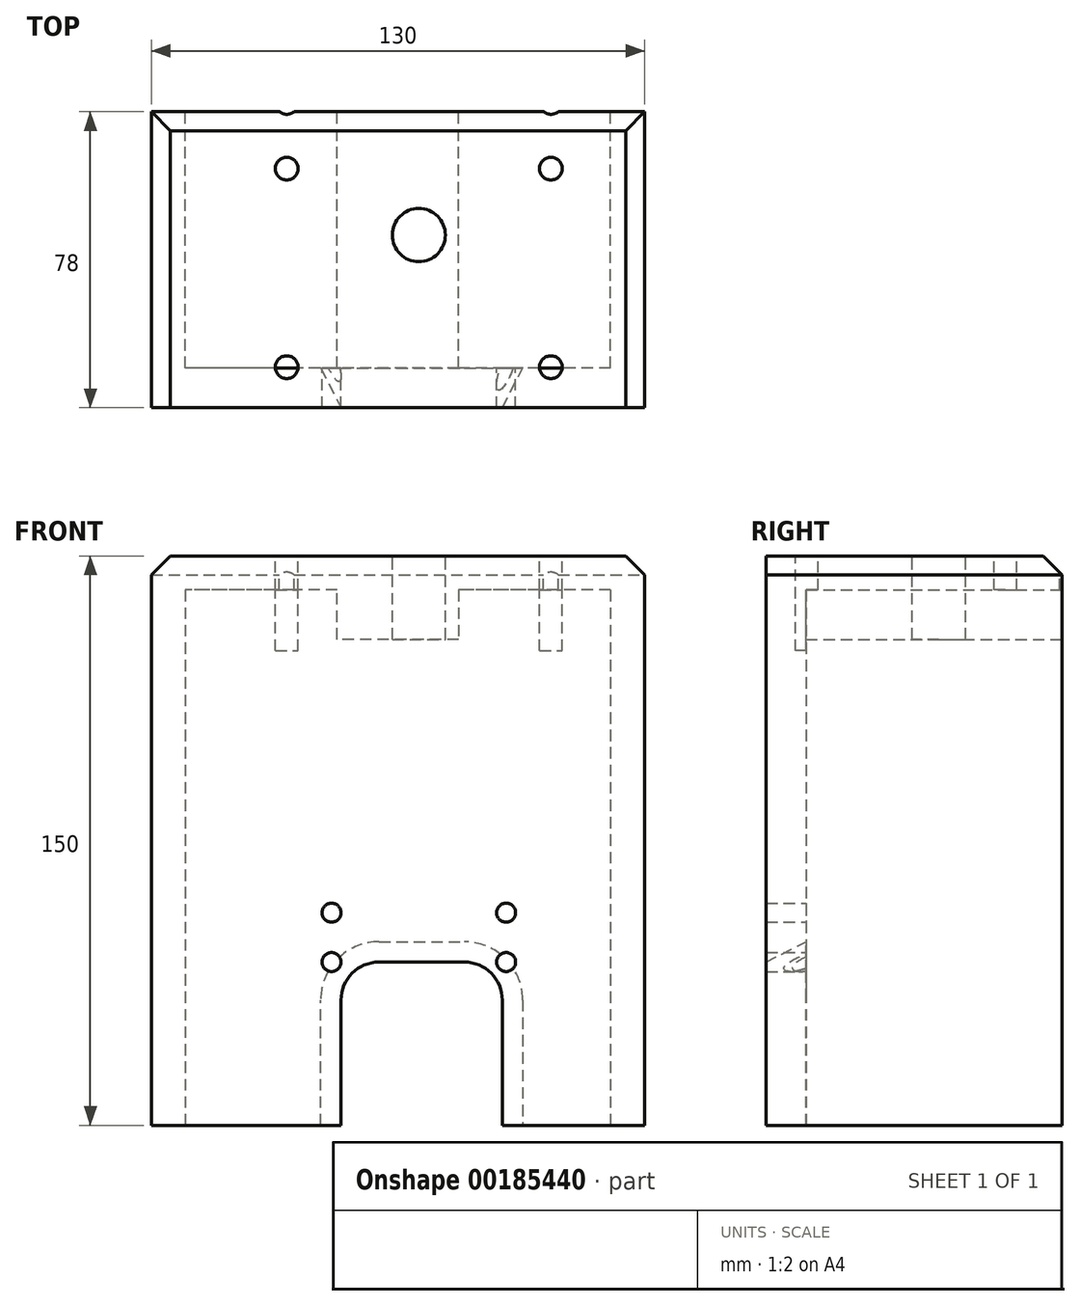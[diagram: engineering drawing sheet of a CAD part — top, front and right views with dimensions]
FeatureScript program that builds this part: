
annotation { "Feature Type Name" : "Feature", "Feature Type Description" : "" }
export const myFeature = defineFeature(function(context is Context, id is Id, definition is map)
    precondition{}
    {
        {
            var Q0;
            Q0=qCreatedBy(makeId("Top.planeOp"),FACE);
            var sketch = newSketch(context, id + "F0", { "sketchPlane" : qUnion([Q0])});
            skLineSegment(sketch, "E0.bottom", {"start": v(65, 39) * mm, "end": v(-65, 39) * mm});
            skLineSegment(sketch, "E0.top", {"start": v(65, -39) * mm, "end": v(-65, -39) * mm});
            skLineSegment(sketch, "E0.left", {"start": v(65, 39) * mm, "end": v(65, -39) * mm});
            skLineSegment(sketch, "E0.right", {"start": v(-65, 39) * mm, "end": v(-65, -39) * mm});
            skPoint(sketch, "E0.middle", {"position": v(0, 0) * mm});
            skSolve(sketch);
        }
        {
            var Q0;
            Q0=makeQuery(id+"F0.imprint","IMPRINT",FACE,{"disambiguationData":[TD([[makeQuery(id+"F0.imprint","IMPRINT",EDGE,{"derivedFrom":sQuery(id+"F0.wireOp",EDGE,"E0.bottom")}),1.0]])]});
            extrude(context, id + "F14", {"entities" : qUnion([Q0]), "oppositeDirection" : true, "depth" : 150 * mm});
        }
        {
            var Q0;
            Q0=makeQuery(id+"F14.opExtrude","SWEPT_FACE",FACE,{"disambiguationData":[OSD([sQuery(id+"F0.wireOp",EDGE,"E0.bottom")])]});
            var sketch = newSketch(context, id + "F15", { "sketchPlane" : qUnion([Q0])});
            skLineSegment(sketch, "E1.bottom", {"start": v(-56, -9) * mm, "end": v(-16, -9) * mm});
            skLineSegment(sketch, "E1.top", {"start": v(-56, -150) * mm, "end": v(56, -150) * mm});
            skLineSegment(sketch, "E1.left", {"start": v(-56, -9) * mm, "end": v(-56, -150) * mm});
            skLineSegment(sketch, "E1.right", {"start": v(56, -9) * mm, "end": v(56, -150) * mm});
            skLineSegment(sketch, "E2", {"start": v(-16, -9) * mm, "end": v(-16, -22) * mm});
            skLineSegment(sketch, "E3", {"start": v(-16, -22) * mm, "end": v(16, -22) * mm});
            skLineSegment(sketch, "E4", {"start": v(16, -22) * mm, "end": v(16, -9) * mm});
            skLineSegment(sketch, "E5.trimOffspring", {"start": v(16, -9) * mm, "end": v(56, -9) * mm});
            skSolve(sketch);
        }
        {
            var Q0;
            Q0=makeQuery(id+"F14.opExtrude","CAP_EDGE",EDGE,{"disambiguationData":[OSD([sQuery(id+"F0.wireOp",EDGE,"E0.left")])],"isStart":true});
            var Q1;
            Q1=makeQuery(id+"F14.opExtrude","CAP_EDGE",EDGE,{"disambiguationData":[OSD([sQuery(id+"F0.wireOp",EDGE,"E0.right")])],"isStart":true});
            var Q2;
            Q2=makeQuery(id+"F14.opExtrude","CAP_EDGE",EDGE,{"disambiguationData":[OSD([sQuery(id+"F0.wireOp",EDGE,"E0.bottom")])],"isStart":true});
            chamfer(context, id + "F1", {"entities" : qUnion([Q0, Q1, Q2]), "width" : 5 * mm, "tangentPropagation" : true});
        }
        {
            var Q0;
            Q0=makeQuery(id+"F15.imprint","IMPRINT",FACE,{"disambiguationData":[TD([[makeQuery(id+"F15.imprint","IMPRINT",EDGE,{"derivedFrom":sQuery(id+"F15.wireOp",EDGE,"E1.bottom")}),-1.0]])]});
            extrude(context, id + "F2", {"entities" : qUnion([Q0]), "operationType" : NewBodyOperationType.REMOVE, "oppositeDirection" : true, "depth" : 67.5 * mm});
        }
        {
            var Q0;
            Q0=makeQuery(id+"F14.opExtrude","CAP_FACE",FACE,{"disambiguationData":[OSD([sQuery(id+"F0.wireOp",EDGE,"E0.bottom"),sQuery(id+"F0.wireOp",EDGE,"E0.top"),sQuery(id+"F0.wireOp",EDGE,"E0.left"),sQuery(id+"F0.wireOp",EDGE,"E0.right")])],"isStart":true});
            var sketch = newSketch(context, id + "F3", { "sketchPlane" : qUnion([Q0])});
            skCircle(sketch, "E6", {"center": v(-34.8, -29) * mm, "radius": 3 * mm});
            skCircle(sketch, "E7", {"center": v(-34.8, 40.6) * mm, "radius": 3 * mm});
            skPoint(sketch, "E8.center.orphan", {"position": v(0, 5.8) * mm});
            skSolve(sketch);
        }
        {
            var Q0;
            Q0=makeQuery(id+"F3.imprint","IMPRINT",FACE,{"disambiguationData":[TD([[makeQuery(id+"F3.imprint","IMPRINT",EDGE,{"derivedFrom":sQuery(id+"F3.wireOp",EDGE,"E6")}),-1.0]])]});
            var sketch = newSketch(context, id + "F4", { "sketchPlane" : qUnion([Q0])});
            skCircle(sketch, "E9", {"center": v(5.5, 6.5) * mm, "radius": 6 * mm});
            skSolve(sketch);
        }
        {
            var Q0;
            Q0=makeQuery(id+"F4.imprint","IMPRINT",FACE,{"disambiguationData":[TD([[makeQuery(id+"F4.imprint","IMPRINT",EDGE,{"derivedFrom":sQuery(id+"F4.wireOp",EDGE,"E9")}),1.0]])]});
            extrude(context, id + "F5", {"entities" : qUnion([Q0]), "operationType" : NewBodyOperationType.REMOVE, "endBound" : BoundingType.THROUGH_ALL, "oppositeDirection" : true, "depth" : 25 * mm});
        }
        {
            var Q0;
            Q0=makeQuery(id+"F14.opExtrude","CAP_FACE",FACE,{"disambiguationData":[OSD([sQuery(id+"F0.wireOp",EDGE,"E0.bottom"),sQuery(id+"F0.wireOp",EDGE,"E0.top"),sQuery(id+"F0.wireOp",EDGE,"E0.left"),sQuery(id+"F0.wireOp",EDGE,"E0.right")])],"isStart":true});
            var sketch = newSketch(context, id + "F6", { "sketchPlane" : qUnion([Q0])});
            skCircle(sketch, "E10", {"center": v(5.5, 6.5) * mm, "radius": 7 * mm});
            skCircle(sketch, "E11", {"center": v(-29.3, -28.3) * mm, "radius": 3 * mm});
            skCircle(sketch, "E12", {"center": v(-29.3, 41.3) * mm, "radius": 3 * mm});
            skCircle(sketch, "E13", {"center": v(40.3, 41.3) * mm, "radius": 3 * mm});
            skCircle(sketch, "E14", {"center": v(40.3, -28.3) * mm, "radius": 3 * mm});
            skSolve(sketch);
        }
        {
            var Q0;
            Q0 = qSketchRegion(id + "F6", true);
            extrude(context, id + "F7", {"entities" : qUnion([Q0]), "operationType" : NewBodyOperationType.REMOVE, "oppositeDirection" : true, "depth" : 25 * mm});
        }
        {
            var Q0;
            Q0=qCreatedBy(makeId("Right.planeOp"),FACE);
            var Q1;
            Q1=sQuery(id+"F6.wireOp",VERTEX,"E10.center");
            cPlane(context, id + "F8", {"entities" : qUnion([Q0, Q1]), "cplaneType" : CPlaneType.PLANE_POINT, "offset" : 25 * mm, "width" : 150 * mm, "height" : 150 * mm});
        }
        {
            var Q0;
            Q0=makeQuery(id+"F2.boolean.opBoolean","COPY",FACE,{"derivedFrom":makeQuery(id+"F2.opExtrude","CAP_FACE",FACE,{"disambiguationData":[OSD([sQuery(id+"F15.wireOp",EDGE,"E1.bottom"),sQuery(id+"F15.wireOp",EDGE,"E1.top"),sQuery(id+"F15.wireOp",EDGE,"E1.left"),sQuery(id+"F15.wireOp",EDGE,"E1.right"),sQuery(id+"F15.wireOp",EDGE,"E2"),sQuery(id+"F15.wireOp",EDGE,"E3"),sQuery(id+"F15.wireOp",EDGE,"E4"),sQuery(id+"F15.wireOp",EDGE,"E5.trimOffspring")])],"isStart":false})});
            var sketch = newSketch(context, id + "F9", { "sketchPlane" : qUnion([Q0])});
            skCircle(sketch, "E15", {"center": v(-28.5, -94) * mm, "radius": 2.5 * mm});
            skCircle(sketch, "E16", {"center": v(-28.5, -107) * mm, "radius": 2.5 * mm});
            skCircle(sketch, "E17.MirrorC", {"center": v(17.5, -94) * mm, "radius": 2.5 * mm});
            skCircle(sketch, "E18.MirrorC", {"center": v(17.5, -107) * mm, "radius": 2.5 * mm});
            skSolve(sketch);
        }
        {
            var Q0;
            Q0 = qSketchRegion(id + "F9", true);
            extrude(context, id + "F10", {"entities" : qUnion([Q0]), "operationType" : NewBodyOperationType.REMOVE, "endBound" : BoundingType.THROUGH_ALL, "oppositeDirection" : true, "depth" : 25 * mm});
        }
        {
            var Q0;
            Q0=makeQuery(id+"F14.opExtrude","SWEPT_FACE",FACE,{"disambiguationData":[OSD([sQuery(id+"F0.wireOp",EDGE,"E0.top")])]});
            var sketch = newSketch(context, id + "F16", { "sketchPlane" : qUnion([Q0])});
            skLineSegment(sketch, "E19.bottom", {"start": v(-5, -107) * mm, "end": v(17.5, -107) * mm});
            skLineSegment(sketch, "E19.top", {"start": v(-15, -150) * mm, "end": v(27.5, -150) * mm});
            skLineSegment(sketch, "E19.left", {"start": v(-15, -117) * mm, "end": v(-15, -150) * mm});
            skLineSegment(sketch, "E19.right", {"start": v(27.5, -117) * mm, "end": v(27.5, -150) * mm});
            skPoint(sketch, "E20.visualSharp", {"position": v(-15, -107) * mm});
            skArc(sketch, "E20.filletArc", {"start": v(-5, -107) * mm, "mid": v(-12.07, -109.93) * mm, "end": v(-15, -117) * mm});
            skPoint(sketch, "E21.visualSharp", {"position": v(27.5, -107) * mm});
            skArc(sketch, "E21.filletArc", {"start": v(27.5, -117) * mm, "mid": v(24.57, -109.93) * mm, "end": v(17.5, -107) * mm});
            skSolve(sketch);
        }
        {
            var Q0;
            Q0=makeQuery(id+"F16.imprint","IMPRINT",FACE,{"disambiguationData":[TD([[makeQuery(id+"F16.imprint","IMPRINT",EDGE,{"derivedFrom":sQuery(id+"F16.wireOp",EDGE,"E19.bottom")}),-1.0]])]});
            extrude(context, id + "F11", {"entities" : qUnion([Q0]), "operationType" : NewBodyOperationType.REMOVE, "oppositeDirection" : true, "depth" : 25 * mm, "hasDraft" : true, "draftAngle" : 27 * degree});
        }
        {
            var Q0;
            Q0=makeQuery(id+"F14.opExtrude","CAP_FACE",FACE,{"disambiguationData":[OSD([sQuery(id+"F0.wireOp",EDGE,"E0.bottom"),sQuery(id+"F0.wireOp",EDGE,"E0.top"),sQuery(id+"F0.wireOp",EDGE,"E0.left"),sQuery(id+"F0.wireOp",EDGE,"E0.right")])],"isStart":true});
            var sketch = newSketch(context, id + "F12", { "sketchPlane" : qUnion([Q0])});
            skCircle(sketch, "E22", {"center": v(-29.3, 24) * mm, "radius": 3 * mm});
            skCircle(sketch, "E23", {"center": v(40.3, 24) * mm, "radius": 3 * mm});
            skSolve(sketch);
        }
        {
            var Q0;
            Q0=makeQuery(id+"F12.imprint","IMPRINT",FACE,{"disambiguationData":[TD([[makeQuery(id+"F12.imprint","IMPRINT",EDGE,{"derivedFrom":sQuery(id+"F12.wireOp",EDGE,"E22")}),1.0]])]});
            var Q1;
            Q1=makeQuery(id+"F12.imprint","IMPRINT",FACE,{"disambiguationData":[TD([[makeQuery(id+"F12.imprint","IMPRINT",EDGE,{"derivedFrom":sQuery(id+"F12.wireOp",EDGE,"E23")}),1.0]])]});
            extrude(context, id + "F13", {"entities" : qUnion([Q0, Q1]), "operationType" : NewBodyOperationType.REMOVE, "oppositeDirection" : true, "depth" : 25 * mm});
        }
    });
